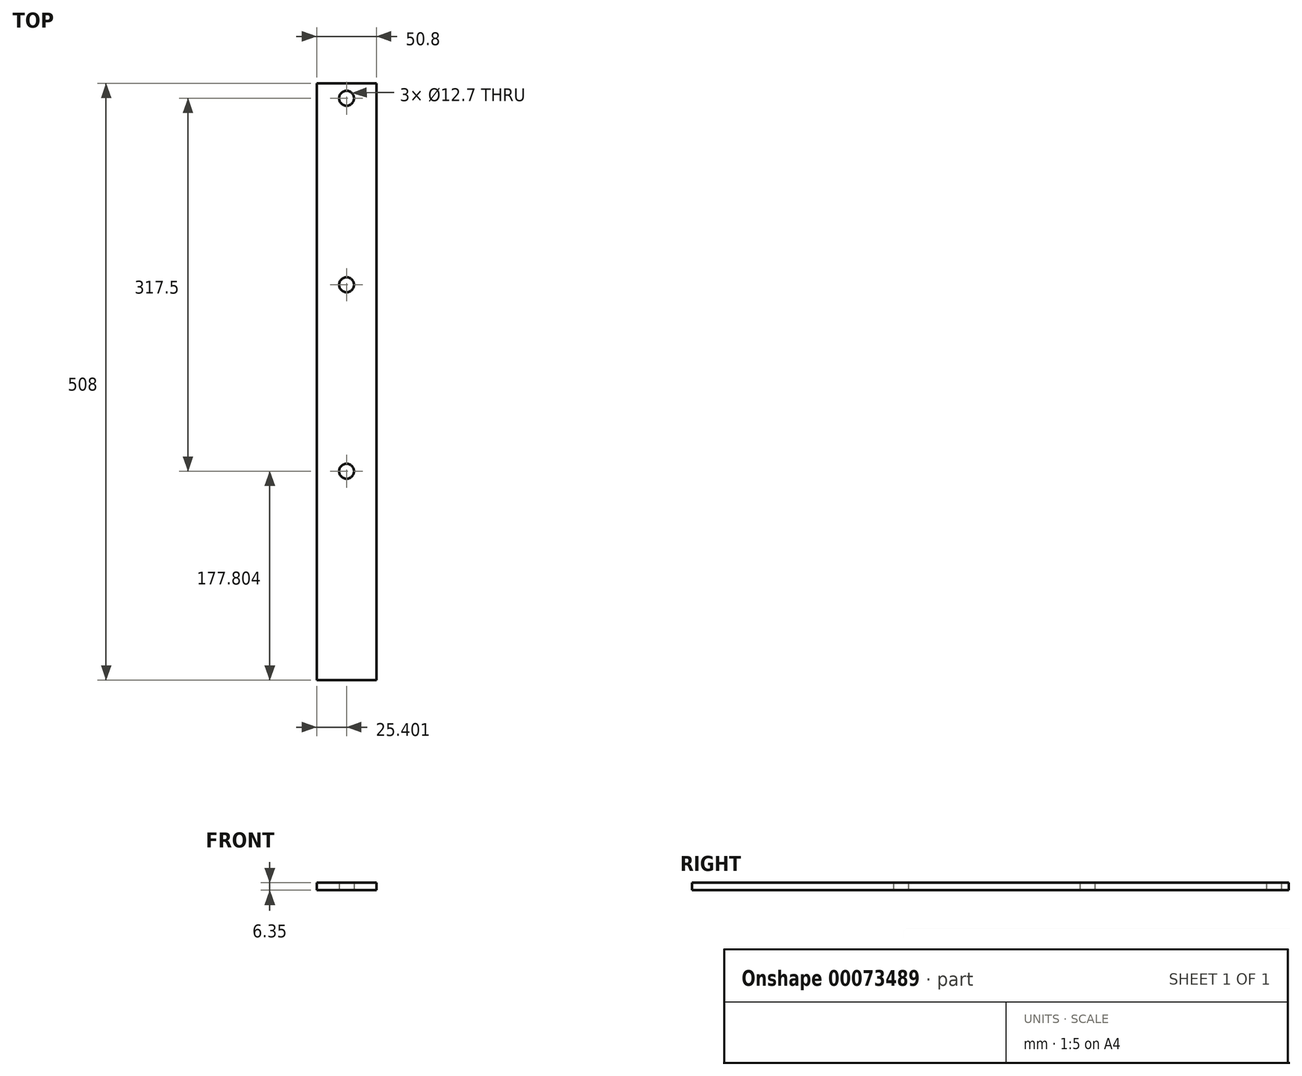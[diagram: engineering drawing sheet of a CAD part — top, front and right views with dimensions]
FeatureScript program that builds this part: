
annotation { "Feature Type Name" : "Feature", "Feature Type Description" : "" }
export const myFeature = defineFeature(function(context is Context, id is Id, definition is map)
    precondition{}
    {
        {
            var Q0;
            Q0=qCreatedBy(makeId("Top.planeOp"),FACE);
            var sketch = newSketch(context, id + "F0", { "sketchPlane" : qUnion([Q0])});
            skLineSegment(sketch, "E0.bottom", {"start": v(-36.77, -35.1) * mm, "end": v(14.03, -35.1) * mm});
            skLineSegment(sketch, "E0.top", {"start": v(-36.77, 472.9) * mm, "end": v(14.03, 472.9) * mm});
            skLineSegment(sketch, "E0.left", {"start": v(-36.77, -35.1) * mm, "end": v(-36.77, 472.9) * mm});
            skLineSegment(sketch, "E0.right", {"start": v(14.03, -35.1) * mm, "end": v(14.03, 472.9) * mm});
            skCircle(sketch, "E1", {"center": v(-11.37, 460.2) * mm, "radius": 6.35 * mm});
            skPoint(sketch, "E1.centerSnap0", {"position": v(-11.37, 472.9) * mm});
            skCircle(sketch, "E2", {"center": v(-11.37, 301.45) * mm, "radius": 6.35 * mm});
            skCircle(sketch, "E3", {"center": v(-11.37, 142.7) * mm, "radius": 6.35 * mm});
            skSolve(sketch);
        }
        {
            var Q0;
            Q0=makeQuery(id+"F0.imprint","IMPRINT",FACE,{"disambiguationData":[TD([[makeQuery(id+"F0.imprint","IMPRINT",EDGE,{"derivedFrom":sQuery(id+"F0.wireOp",EDGE,"E0.bottom")}),1.0]])]});
            extrude(context, id + "F1", {"entities" : qUnion([Q0]), "depth" : 6.35 * mm});
        }
    });
